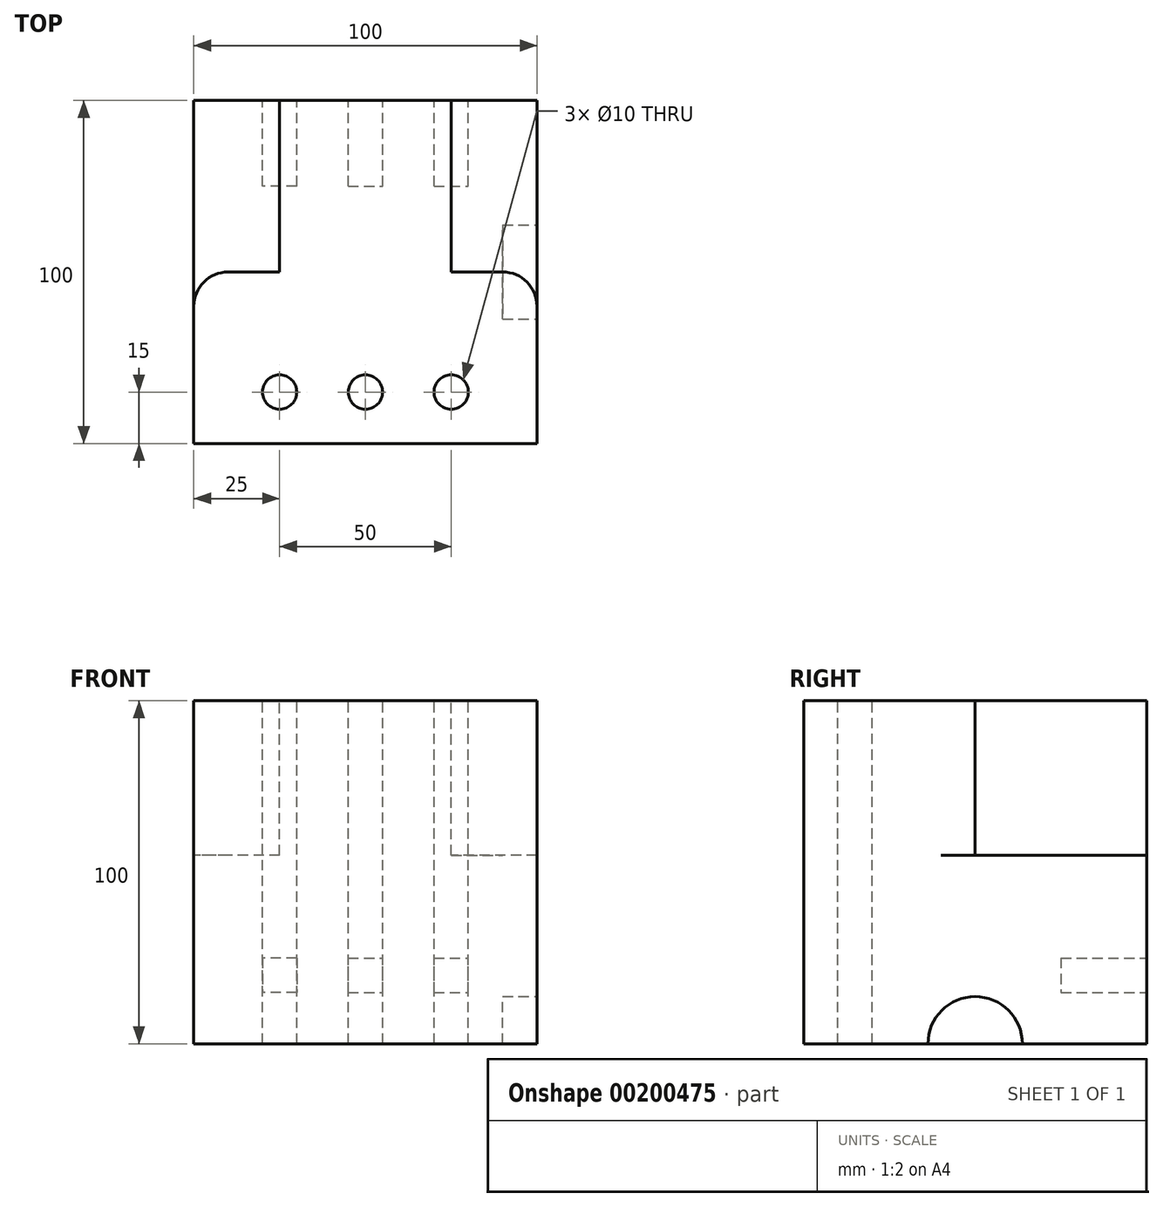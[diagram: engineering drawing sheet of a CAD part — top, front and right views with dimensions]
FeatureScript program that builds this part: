
annotation { "Feature Type Name" : "Feature", "Feature Type Description" : "" }
export const myFeature = defineFeature(function(context is Context, id is Id, definition is map)
    precondition{}
    {
        {
            var Q0;
            Q0=qCreatedBy(makeId("Right.planeOp"),FACE);
            var sketch = newSketch(context, id + "F0", { "sketchPlane" : qUnion([Q0])});
            skLineSegment(sketch, "E0", {"start": v(0, 0) * mm, "end": v(100, 0) * mm});
            skLineSegment(sketch, "E1", {"start": v(100, 0) * mm, "end": v(100, 100) * mm});
            skLineSegment(sketch, "E2", {"start": v(100, 100) * mm, "end": v(0, 100) * mm});
            skLineSegment(sketch, "E3", {"start": v(0, 100) * mm, "end": v(0, 0) * mm});
            skSolve(sketch);
        }
        {
            var Q0;
            Q0 = qSketchRegion(id + "F0", true);
            extrude(context, id + "F1", {"entities" : qUnion([Q0]), "depth" : 100 * mm});
        }
        {
            var Q0;
            Q0=makeQuery(id+"F1.opExtrude","CAP_FACE",FACE,{"disambiguationData":[OSD([sQuery(id+"F0.wireOp",EDGE,"E0"),sQuery(id+"F0.wireOp",EDGE,"E1"),sQuery(id+"F0.wireOp",EDGE,"E2"),sQuery(id+"F0.wireOp",EDGE,"E3")])],"isStart":false});
            var sketch = newSketch(context, id + "F2", { "sketchPlane" : qUnion([Q0])});
            skArc(sketch, "E4", {"start": v(63.75, 0) * mm, "mid": v(50, 13.75) * mm, "end": v(36.25, 0) * mm});
            skSolve(sketch);
        }
        {
            var Q0;
            {var subQ0=sQuery(id+"F2.wireOp",EDGE,"E4");Q0=makeQuery(id+"F2.imprint","IMPRINT",FACE,{"disambiguationData":[TD([[makeQuery(id+"F2.imprint","IMPRINT",EDGE,{"derivedFrom":subQ0}),1.0]])]});}
            extrude(context, id + "F3", {"entities" : qUnion([Q0]), "operationType" : NewBodyOperationType.REMOVE, "oppositeDirection" : true, "depth" : 10 * mm});
        }
        {
            var Q0;
            Q0=makeQuery(id+"F1.opExtrude","SWEPT_FACE",FACE,{"disambiguationData":[OSD([sQuery(id+"F0.wireOp",EDGE,"E2")])]});
            var sketch = newSketch(context, id + "F4", { "sketchPlane" : qUnion([Q0])});
            skLineSegment(sketch, "E5", {"start": v(75, 100) * mm, "end": v(75, 50) * mm});
            skLineSegment(sketch, "E6", {"start": v(75, 50) * mm, "end": v(90, 50) * mm});
            skLineSegment(sketch, "E7", {"start": v(25, 100) * mm, "end": v(25, 50) * mm});
            skLineSegment(sketch, "E8", {"start": v(25, 50) * mm, "end": v(10, 50) * mm});
            skLineSegment(sketch, "E9", {"start": v(0, 40) * mm, "end": v(0, 0) * mm});
            skLineSegment(sketch, "E10", {"start": v(100, 40) * mm, "end": v(100, 0) * mm});
            skPoint(sketch, "E11.visualSharp", {"position": v(0, 50) * mm});
            skArc(sketch, "E11.filletArc", {"start": v(10, 50) * mm, "mid": v(2.93, 47.07) * mm, "end": v(0, 40) * mm});
            skPoint(sketch, "E12.visualSharp", {"position": v(100, 50) * mm});
            skArc(sketch, "E12.filletArc", {"start": v(100, 40) * mm, "mid": v(97.07, 47.07) * mm, "end": v(90, 50) * mm});
            skSolve(sketch);
        }
        {
            var Q0;
            {var subQ5=sQuery(id+"F4.wireOp",EDGE,"E7");Q0=makeQuery(id+"F4.imprint","IMPRINT",FACE,{"disambiguationData":[TD([[makeQuery(id+"F4.imprint","IMPRINT",EDGE,{"derivedFrom":subQ5}),-1.0]])]});}
            var Q1;
            {var subQ5=sQuery(id+"F4.wireOp",EDGE,"E5");Q1=makeQuery(id+"F4.imprint","IMPRINT",FACE,{"disambiguationData":[TD([[makeQuery(id+"F4.imprint","IMPRINT",EDGE,{"derivedFrom":subQ5}),1.0]])]});}
            extrude(context, id + "F5", {"entities" : qUnion([Q0, Q1]), "operationType" : NewBodyOperationType.REMOVE, "oppositeDirection" : true, "depth" : 45 * mm});
        }
        {
            var Q0;
            Q0=makeQuery(id+"F1.opExtrude","SWEPT_FACE",FACE,{"disambiguationData":[OSD([sQuery(id+"F0.wireOp",EDGE,"E2")])]});
            var sketch = newSketch(context, id + "F6", { "sketchPlane" : qUnion([Q0])});
            skCircle(sketch, "E13", {"center": v(25, 15) * mm, "radius": 5 * mm});
            skCircle(sketch, "E14", {"center": v(50, 15) * mm, "radius": 5 * mm});
            skCircle(sketch, "E15", {"center": v(75, 15) * mm, "radius": 5 * mm});
            skSolve(sketch);
        }
        {
            var Q0;
            Q0=makeQuery(id+"F6.imprint","IMPRINT",FACE,{"disambiguationData":[TD([[makeQuery(id+"F6.imprint","IMPRINT",EDGE,{"derivedFrom":sQuery(id+"F6.wireOp",EDGE,"E13")}),1.0]])]});
            var Q1;
            Q1=makeQuery(id+"F6.imprint","IMPRINT",FACE,{"disambiguationData":[TD([[makeQuery(id+"F6.imprint","IMPRINT",EDGE,{"derivedFrom":sQuery(id+"F6.wireOp",EDGE,"E15")}),1.0]])]});
            var Q2;
            Q2=makeQuery(id+"F6.imprint","IMPRINT",FACE,{"disambiguationData":[TD([[makeQuery(id+"F6.imprint","IMPRINT",EDGE,{"derivedFrom":sQuery(id+"F6.wireOp",EDGE,"E14")}),1.0]])]});
            var Q3;
            Q3=sQuery(id+"F6.wireOp",EDGE,"E13");
            var Q4;
            Q4=sQuery(id+"F6.wireOp",EDGE,"E14");
            var Q5;
            Q5=sQuery(id+"F6.wireOp",EDGE,"E15");
            extrude(context, id + "F7", {"entities" : qUnion([Q0, Q1, Q2]), "operationType" : NewBodyOperationType.REMOVE, "surfaceEntities" : qUnion([Q3, Q4, Q5]), "endBound" : BoundingType.THROUGH_ALL, "oppositeDirection" : true, "depth" : 25 * mm});
        }
        {
            var Q0;
            Q0=makeQuery(id+"F1.opExtrude","SWEPT_FACE",FACE,{"disambiguationData":[OSD([sQuery(id+"F0.wireOp",EDGE,"E1")])]});
            var sketch = newSketch(context, id + "F8", { "sketchPlane" : qUnion([Q0])});
            skLineSegment(sketch, "E16.bottom", {"start": v(-70, 15) * mm, "end": v(-80, 15) * mm});
            skLineSegment(sketch, "E16.top", {"start": v(-70, 25) * mm, "end": v(-80, 25) * mm});
            skLineSegment(sketch, "E16.left", {"start": v(-70, 15) * mm, "end": v(-70, 25) * mm});
            skLineSegment(sketch, "E16.right", {"start": v(-80, 15) * mm, "end": v(-80, 25) * mm});
            skPoint(sketch, "E16.middle", {"position": v(-75, 20) * mm});
            skLineSegment(sketch, "E17.bottom", {"start": v(-45, 15) * mm, "end": v(-55, 15) * mm});
            skLineSegment(sketch, "E17.top", {"start": v(-45, 25) * mm, "end": v(-55, 25) * mm});
            skLineSegment(sketch, "E17.left", {"start": v(-45, 15) * mm, "end": v(-45, 25) * mm});
            skLineSegment(sketch, "E17.right", {"start": v(-55, 15) * mm, "end": v(-55, 25) * mm});
            skPoint(sketch, "E17.middle", {"position": v(-50, 20) * mm});
            skLineSegment(sketch, "E18.bottom", {"start": v(-30, 25) * mm, "end": v(-20, 25) * mm});
            skLineSegment(sketch, "E18.top", {"start": v(-30, 15) * mm, "end": v(-20, 15) * mm});
            skLineSegment(sketch, "E18.left", {"start": v(-30, 25) * mm, "end": v(-30, 15) * mm});
            skLineSegment(sketch, "E18.right", {"start": v(-20, 25) * mm, "end": v(-20, 15) * mm});
            skPoint(sketch, "E18.middle", {"position": v(-25, 20) * mm});
            skSolve(sketch);
        }
        {
            var Q0;
            Q0=makeQuery(id+"F8.imprint","IMPRINT",FACE,{"disambiguationData":[TD([[makeQuery(id+"F8.imprint","IMPRINT",EDGE,{"derivedFrom":sQuery(id+"F8.wireOp",EDGE,"E16.bottom")}),-1.0]])]});
            var Q1;
            Q1=makeQuery(id+"F8.imprint","IMPRINT",FACE,{"disambiguationData":[TD([[makeQuery(id+"F8.imprint","IMPRINT",EDGE,{"derivedFrom":sQuery(id+"F8.wireOp",EDGE,"E17.bottom")}),-1.0]])]});
            var Q2;
            Q2=makeQuery(id+"F8.imprint","IMPRINT",FACE,{"disambiguationData":[TD([[makeQuery(id+"F8.imprint","IMPRINT",EDGE,{"derivedFrom":sQuery(id+"F8.wireOp",EDGE,"E18.bottom")}),-1.0]])]});
            extrude(context, id + "F9", {"entities" : qUnion([Q0, Q1, Q2]), "operationType" : NewBodyOperationType.REMOVE, "oppositeDirection" : true, "depth" : 25 * mm});
        }
    });
